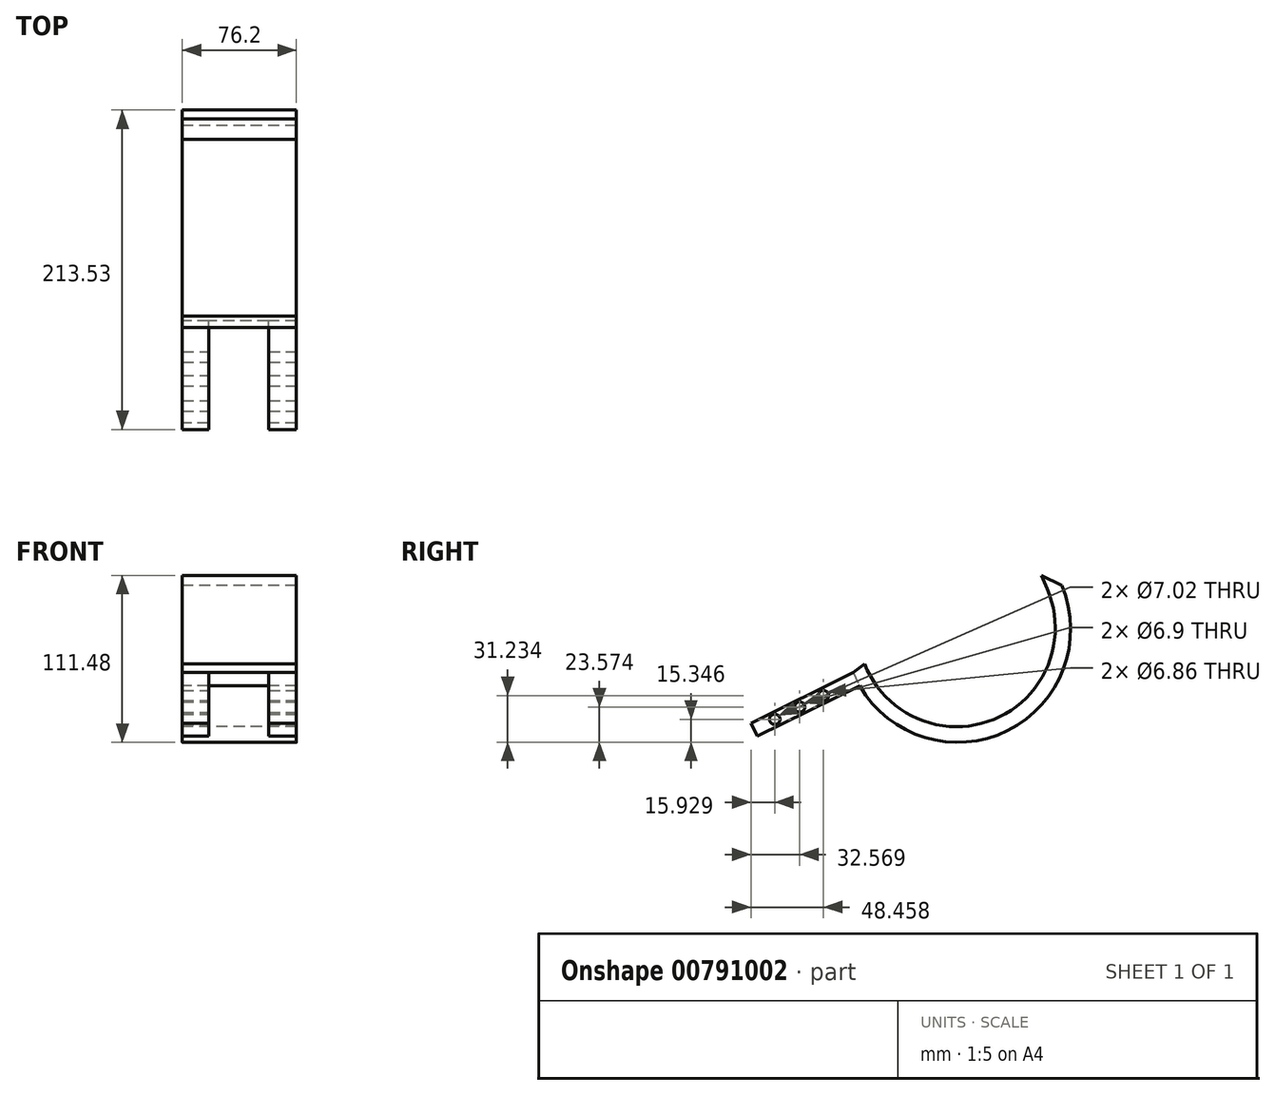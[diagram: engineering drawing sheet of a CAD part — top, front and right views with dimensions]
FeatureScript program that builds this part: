
annotation { "Feature Type Name" : "Feature", "Feature Type Description" : "" }
export const myFeature = defineFeature(function(context is Context, id is Id, definition is map)
    precondition{}
    {
        {
            var Q0;
            Q0=qCreatedBy(makeId("Right.planeOp"),FACE);
            var sketch = newSketch(context, id + "F0", { "sketchPlane" : qUnion([Q0])});
            skArc(sketch, "E0", {"start": v(-39.2, -3.85) * mm, "mid": v(59.72, -33.72) * mm, "end": v(95.76, 63.13) * mm});
            skArc(sketch, "E1", {"start": v(-35.97, 10.92) * mm, "mid": v(50.47, -26.26) * mm, "end": v(86.03, 60.86) * mm});
            skLineSegment(sketch, "E2", {"start": v(86.03, 60.86) * mm, "end": v(82.14, 69.89) * mm});
            skLineSegment(sketch, "E3", {"start": v(82.14, 69.89) * mm, "end": v(95.76, 63.13) * mm});
            skLineSegment(sketch, "E4", {"start": v(-43.55, 4.97) * mm, "end": v(-35.97, 10.92) * mm});
            skPoint(sketch, "E5.start.orphan", {"position": v(-107.47, 4.97) * mm});
            skLineSegment(sketch, "E6", {"start": v(-43.55, 4.97) * mm, "end": v(-39.2, -3.85) * mm});
            skSolve(sketch);
        }
        {
            var Q0;
            Q0 = qSketchRegion(id + "F0", true);
            extrude(context, id + "F1", {"entities" : qUnion([Q0]), "depth" : 76.2 * mm, "offsetDistance" : 25.4 * mm});
        }
        {
            var Q0;
            Q0=makeQuery(id+"F1.opExtrude","SWEPT_FACE",FACE,{"disambiguationData":[OSD([sQuery(id+"F0.wireOp",EDGE,"E6")])]});
            var sketch = newSketch(context, id + "F2", { "sketchPlane" : qUnion([Q0])});
            skLineSegment(sketch, "E7.bottom", {"start": v(0, 23.73) * mm, "end": v(17.67, 23.73) * mm});
            skLineSegment(sketch, "E7.top", {"start": v(0, 13.9) * mm, "end": v(17.67, 13.9) * mm});
            skLineSegment(sketch, "E7.left", {"start": v(0, 23.73) * mm, "end": v(0, 13.9) * mm});
            skLineSegment(sketch, "E7.right", {"start": v(17.67, 23.73) * mm, "end": v(17.67, 13.9) * mm});
            skLineSegment(sketch, "E8.bottom", {"start": v(76.2, 23.73) * mm, "end": v(57.68, 23.73) * mm});
            skLineSegment(sketch, "E8.top", {"start": v(76.2, 13.9) * mm, "end": v(57.68, 13.9) * mm});
            skLineSegment(sketch, "E8.left", {"start": v(76.2, 23.73) * mm, "end": v(76.2, 13.9) * mm});
            skLineSegment(sketch, "E8.right", {"start": v(57.68, 23.73) * mm, "end": v(57.68, 13.9) * mm});
            skSolve(sketch);
        }
        {
            var Q0;
            Q0 = qSketchRegion(id + "F2", true);
            extrude(context, id + "F3", {"entities" : qUnion([Q0]), "operationType" : NewBodyOperationType.ADD, "depth" : 76.2 * mm, "offsetDistance" : 25.4 * mm});
        }
        {
            var Q0;
            Q0=makeQuery(id+"F3.boolean.opBoolean","MERGE",FACE,{"derivedFrom":[makeQuery(id+"F1.opExtrude","CAP_FACE",FACE,{"disambiguationData":[OSD([sQuery(id+"F0.wireOp",EDGE,"E0"),sQuery(id+"F0.wireOp",EDGE,"E1"),sQuery(id+"F0.wireOp",EDGE,"E2"),sQuery(id+"F0.wireOp",EDGE,"E3"),sQuery(id+"F0.wireOp",EDGE,"E4"),sQuery(id+"F0.wireOp",EDGE,"E6")])],"isStart":false}),makeQuery(id+"F3.opExtrude","SWEPT_FACE",FACE,{"disambiguationData":[OSD([sQuery(id+"F2.wireOp",EDGE,"E8.left")])]})]});
            var sketch = newSketch(context, id + "F4", { "sketchPlane" : qUnion([Q0])});
            skCircle(sketch, "E9", {"center": v(-95.95, -26.24) * mm, "radius": 3.5 * mm});
            skCircle(sketch, "E10", {"center": v(-79.31, -18.02) * mm, "radius": 3.45 * mm});
            skSolve(sketch);
        }
        {
            var Q0;
            Q0=makeQuery(id+"F4.imprint","IMPRINT",FACE,{"disambiguationData":[TD([[makeQuery(id+"F4.imprint","IMPRINT",EDGE,{"derivedFrom":sQuery(id+"F4.wireOp",EDGE,"E10")}),1.0]])]});
            var Q1;
            Q1=makeQuery(id+"F4.imprint","IMPRINT",FACE,{"disambiguationData":[TD([[makeQuery(id+"F4.imprint","IMPRINT",EDGE,{"derivedFrom":sQuery(id+"F4.wireOp",EDGE,"E9")}),1.0]])]});
            var Q2;
            Q2=sQuery(id+"F4.wireOp",EDGE,"E9");
            var Q3;
            Q3=sQuery(id+"F4.wireOp",EDGE,"E10");
            extrude(context, id + "F5", {"entities" : qUnion([Q0, Q1]), "operationType" : NewBodyOperationType.REMOVE, "surfaceEntities" : qUnion([Q2, Q3]), "oppositeDirection" : true, "depth" : 127 * mm, "offsetDistance" : 25.4 * mm});
        }
        {
            var Q0;
            Q0=makeQuery(id+"F3.boolean.opBoolean","MERGE",FACE,{"derivedFrom":[makeQuery(id+"F1.opExtrude","CAP_FACE",FACE,{"disambiguationData":[OSD([sQuery(id+"F0.wireOp",EDGE,"E0"),sQuery(id+"F0.wireOp",EDGE,"E1"),sQuery(id+"F0.wireOp",EDGE,"E2"),sQuery(id+"F0.wireOp",EDGE,"E3"),sQuery(id+"F0.wireOp",EDGE,"E4"),sQuery(id+"F0.wireOp",EDGE,"E6")])],"isStart":false}),makeQuery(id+"F3.opExtrude","SWEPT_FACE",FACE,{"disambiguationData":[OSD([sQuery(id+"F2.wireOp",EDGE,"E8.left")])]})]});
            var sketch = newSketch(context, id + "F6", { "sketchPlane" : qUnion([Q0])});
            skCircle(sketch, "E11", {"center": v(-63.42, -10.36) * mm, "radius": 3.43 * mm});
            skSolve(sketch);
        }
        {
            var Q0;
            Q0 = qSketchRegion(id + "F6", true);
            extrude(context, id + "F7", {"entities" : qUnion([Q0]), "operationType" : NewBodyOperationType.REMOVE, "oppositeDirection" : true, "depth" : 127 * mm, "offsetDistance" : 25.4 * mm});
        }
    });
